# Revit family: LE_C
name_source: partatom
category: Lighting Fixtures
units: mm (PartAtom-declared; Revit-internal decimal feet)

## family parameters
Cut with Voids When Loaded = No
Host = Face
Light Source = Yes
OmniClass Number = 23.80.70.11.21
OmniClass Title = Emergency Lighting
Part Type = Normal
Room Calculation Point = No
Round Connector Dimension = Use Diameter
Shared = No

## types (1)
- LE-White
    Backbox = White
    Color Filter = 16777215
    Default Elevation = 48.000"
    Description = Recessed Mounting Architectural Edge-Lit LED Exit Signs
    Dimming Lamp Color Temperature Shift = <None>
    Emit from Line Length = 13.000"
    Family = Outdoor Emergency Lighting
    Glass = Glass
    Lamp = LED
    Lettering = Red
    Light Source Symbol Size = 0.250"
    Manufacturer = Lifeshield
    Model = LE
    Mounting = Ceiling Mount
    URL = https://www.currentlighting.com
    Wattage Comments = 2.2-5 W

## geometry (parser evidence)
native form markers: Blend x1, Sweep x2
no freeform markers — native parametric forms only
